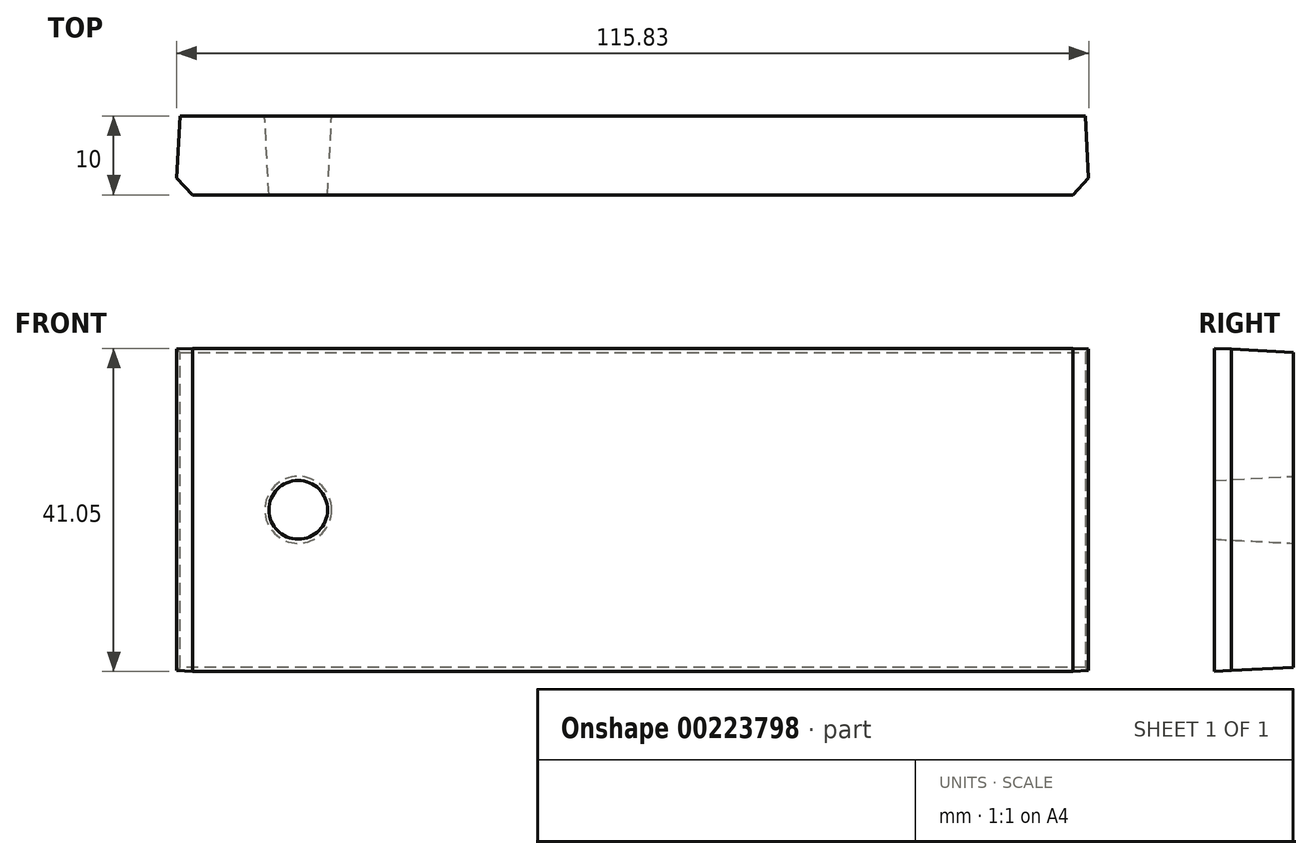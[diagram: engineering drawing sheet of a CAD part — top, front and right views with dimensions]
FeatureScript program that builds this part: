
annotation { "Feature Type Name" : "Feature", "Feature Type Description" : "" }
export const myFeature = defineFeature(function(context is Context, id is Id, definition is map)
    precondition{}
    {
        {
            var Q0;
            Q0=qCreatedBy(makeId("Front.planeOp"),FACE);
            var sketch = newSketch(context, id + "F0", { "sketchPlane" : qUnion([Q0])});
            skLineSegment(sketch, "E0.bottom", {"start": v(-186.15, 37.75) * mm, "end": v(-71.15, 37.75) * mm});
            skLineSegment(sketch, "E0.top", {"start": v(-186.15, -2.25) * mm, "end": v(-71.15, -2.25) * mm});
            skLineSegment(sketch, "E0.left", {"start": v(-186.15, 37.75) * mm, "end": v(-186.15, -2.25) * mm});
            skLineSegment(sketch, "E0.right", {"start": v(-71.15, 37.75) * mm, "end": v(-71.15, -2.25) * mm});
            skLineSegment(sketch, "E1.right", {"start": v(-186.15, 37.75) * mm, "end": v(-186.15, 17.75) * mm});
            skCircle(sketch, "E2", {"center": v(-171.15, 17.75) * mm, "radius": 4.25 * mm});
            skSolve(sketch);
        }
        {
            var Q0;
            Q0=makeQuery(id+"F0.imprint","IMPRINT",FACE,{"disambiguationData":[TD([[makeQuery(id+"F0.imprint","IMPRINT",EDGE,{"derivedFrom":sQuery(id+"F0.wireOp",EDGE,"E0.bottom")}),-1.0]])]});
            extrude(context, id + "F1", {"entities" : qUnion([Q0]), "depth" : 10 * mm, "hasDraft" : true, "draftAngle" : 3 * degree});
        }
        {
            var Q0;
            Q0=makeQuery(id+"F1.opExtrude","CAP_EDGE",EDGE,{"disambiguationData":[OSD([sQuery(id+"F0.wireOp",EDGE,"E0.left"),sQuery(id+"F0.wireOp",EDGE,"E1.right")])],"isStart":false});
            var Q1;
            Q1=makeQuery(id+"F1.opExtrude","CAP_EDGE",EDGE,{"disambiguationData":[OSD([sQuery(id+"F0.wireOp",EDGE,"E0.right")])],"isStart":false});
            chamfer(context, id + "F2", {"entities" : qUnion([Q0, Q1]), "width" : 2 * mm, "tangentPropagation" : true});
        }
    });
